# Revit family: Fixture_Support_Water_Closet_Vertical_Back-to-Back-Zurn-Z1202-ND4-FMBO
name_source: partatom
category: Plumbing Fixtures
units: mm (PartAtom-declared; Revit-internal decimal feet)

## family parameters
Always vertical = Yes
Cut with Voids When Loaded = No
Maintain Annotation Orientation = No
OmniClass Number = 23.45.55.11
OmniClass Title = Sanitary Components
Part Type = Normal
Room Calculation Point = No
Round Connector Dimension = Use Radius
Shared = No
Work Plane-Based = No

## types (1)
- Z1202-ND4-FMBO
    Approx. Weight (Lbs) = 81 "
    Assembly Code = D2030100
    CW Connection = No
    CWFU = 0
    Connector Radius = 2 "
    Coupling Diameter = 3 "
    Coupling Material = ABS - Zurn - Plastic
    Coupling Radius = 1.5 "
    Default Elevation = 20 "
    Description = EZCARRY® ADJUSTABLE VERTICAL HIGH PERFORMANCE BACK-TO-BACK SIPHON JET NO-HUB WATER CLOSET CARRIER SYSTEM W/ FLOOR MOUNT BACK OUTLET FIXTURE SUPPORT
    Dimension "N" = 13.188 "
    Enter Rough In Height = 10 "
    HW Connection = No
    HWFU = 0
    Hardware = Steel - Zurn  - Galvanized
    Main Material = Iron - Zurn - Cast - Painted - Blue
    Manufacturer = Zurn Water, LLC
    Manufacurer Brand = Zurn
    Model = Z1202-ND4-FMBO
    Modified Date = 01/28/2026
    Pipe Size_A Inside Diameter = 4.026 "
    Pipe Size_A Nominal Diameter = 4 "
    Pipe Size_A Nominal Radius = 2 "
    Pipe Size_A Outer Diameter = 4.5 "
    Product Documentation Link = https://files.zurn.com
    Product Installation Sheet URL = https://files.zurn.com
    Product Page URL = https://www.zurn.com
    Product data url = https://www.bimobject.com
    URL = www.zurn.com
    Vent Connection = Yes
    Vent Inner Diameter = 2.067 "
    Vent Inner Radius = 1.034 "
    Vent Nominal Diameter = 2 "
    Vent Nominal Radius = 1 "
    Vent Outer Diameter = 2.375 "
    WFU = 1
    Waste Connection = Yes

## geometry (parser evidence)
native form markers: Blend x10, Sweep x14
no freeform markers — native parametric forms only
